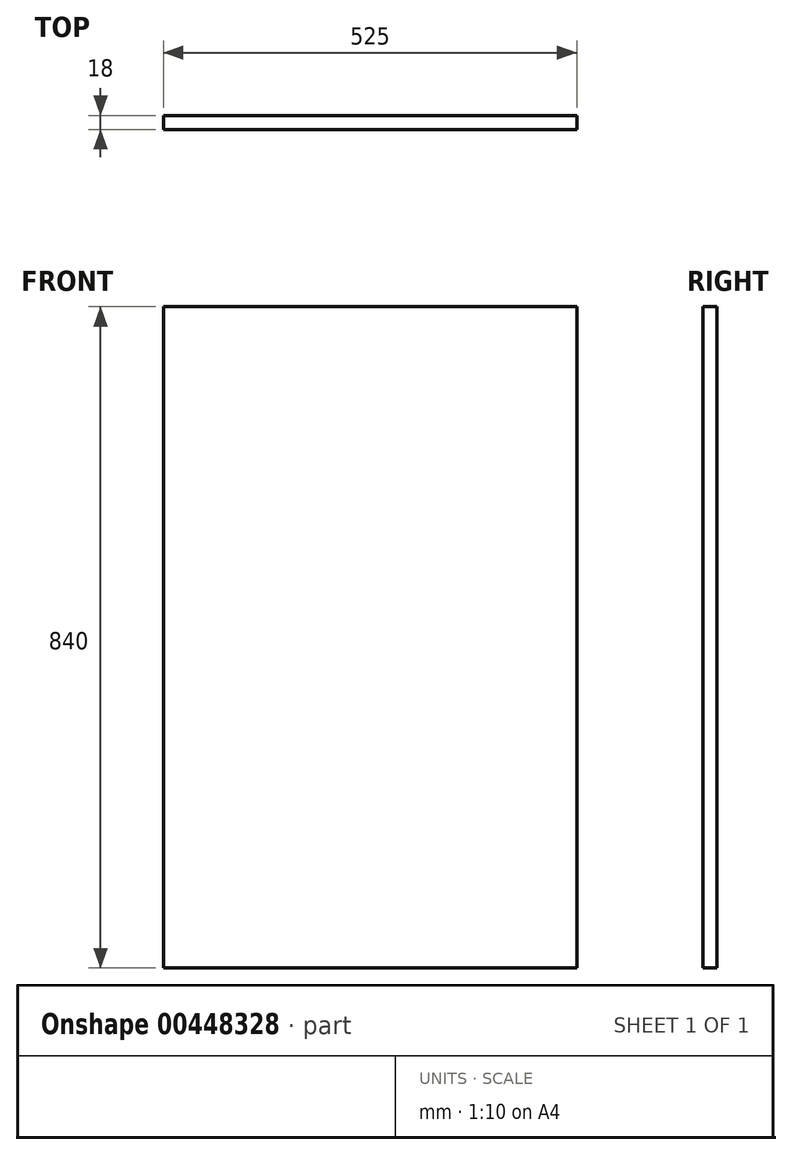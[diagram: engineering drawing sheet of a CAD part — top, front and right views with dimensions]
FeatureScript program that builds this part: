
annotation { "Feature Type Name" : "Feature", "Feature Type Description" : "" }
export const myFeature = defineFeature(function(context is Context, id is Id, definition is map)
    precondition{}
    {
        {
            var Q0;
            Q0=qCreatedBy(makeId("Front.planeOp"),FACE);
            var sketch = newSketch(context, id + "F0", { "sketchPlane" : qUnion([Q0])});
            skLineSegment(sketch, "E0.bottom", {"start": v(0, 0) * mm, "end": v(525, 0) * mm});
            skLineSegment(sketch, "E0.top", {"start": v(0, 840) * mm, "end": v(525, 840) * mm});
            skLineSegment(sketch, "E0.left", {"start": v(0, 0) * mm, "end": v(0, 840) * mm});
            skLineSegment(sketch, "E0.right", {"start": v(525, 0) * mm, "end": v(525, 840) * mm});
            skSolve(sketch);
        }
        {
            var Q0;
            Q0=makeQuery(id+"F0.imprint","IMPRINT",FACE,{"disambiguationData":[TD([[makeQuery(id+"F0.imprint","IMPRINT",EDGE,{"derivedFrom":sQuery(id+"F0.wireOp",EDGE,"E0.bottom")}),1.0]])]});
            extrude(context, id + "F1", {"entities" : qUnion([Q0]), "depth" : 18 * mm});
        }
    });
